# Revit family: Sink-Vessel-Lavatory-KOHLER-MODERN_LIFE-K-77761ID
name_source: partatom
category: Plumbing Fixtures
units: mm (PartAtom-declared; Revit-internal decimal feet)

## family parameters
Cut with Voids When Loaded = No
Enable Cutting in Views = No
Host = Face
Maintain Annotation Orientation = No
OmniClass Number = 23.31.13.00
OmniClass Title = Sinks
Part Type = Normal
Room Calculation Point = No
Round Connector Dimension = Use Diameter
Shared = No

## types (2) — shared parameters
ADA Compliant = No
Assembly Code = D2010400
CW Connection = No
Cold Water Inlet = Cold Water Inlet
Date Modified = 01/29/2026
Default Elevation = 36"
Description = Vessel With Faucet Deck
Drain Included = No
Finish = Kohler-Vitreous_China-0-White
HW Connection = No
Height = 7 1/8"
Hot Water Inlet = Hot Water Inlet
Length = 18 15/16"
Manufacturer = Kohler Co.
Master Format 2014 = 22 41 16
Master Format 2014 Name = Residential Lavatories and Sinks
Material = Vitreous China
Product Name = MODERN LIFE
URL = https://www.kohler.co.id
Vent Connection = No
Waste Connection = Yes
Waste Water Outlet = Waste Water Outlet
WaterSense Certified = No
Width = 23 9/16"

## per-type parameters (varying)
| type | -8 | Faucet Hole Spacing | Model | Type | _1 |
| Single Faucet Hole,0-White | No | 0" | K-77761ID-1-0 | 1 | Yes |
| Three Faucet Hole,0-White | Yes | 8" | K-77761ID-8-0 | 2 | No |

## geometry (parser evidence)
native form markers: Sweep x4
no freeform markers — native parametric forms only
